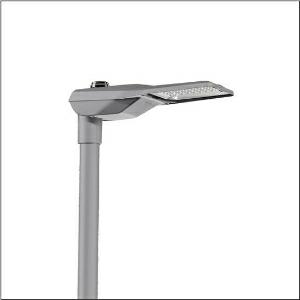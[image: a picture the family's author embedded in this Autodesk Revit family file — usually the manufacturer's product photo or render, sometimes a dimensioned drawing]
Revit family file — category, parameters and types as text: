
# Revit family: streetlight_sl_21_mini___stw1_0a_5xe6e37n08gb_9d35
name_source: partatom
category: Lighting Fixtures
units: mm (PartAtom-declared; Revit-internal decimal feet)

## family parameters
Cut with Voids When Loaded = No
Host = Face
Light Source = No
Part Type = Normal
Room Calculation Point = No
Round Connector Dimension = Use Diameter
Shared = No

## types (1)
- --- (1 x LED, 5940 lm, 40.4 W, 3000K)
    Apparent Load = 40 VA
    CIE Flux Codes = 38 75 98 100 100
    Color Rendering = 70
    Color Temperature = 3000K
    Default Elevation = 1800 mm
    Description = Streetlight SL 21 mini, mast luminaire, primary light control with lens, of PMMA, primary optical cover: cover, of toughened safety glass, transparent, light distribution: STW1.0a, light emission: direct distribution, primary light characteristic: asymmetric, installation type: side-entry, LED, 3G 1.5mm², High Power LED, rated luminous flux: 5.940lm, luminous efficacy: 147lm/W, light colour: 730, colour temperature: 3000K, control gear: NEMA (7pin), control: overheat protection, pre-setting: linear dimming characteristic, constant luminous flux control, time-dependent luminous flux control, flexible luminous flux parameterisation, mains connection: 230..240V, AC, 50/60Hz, connection cable pre-assembled, cable length: 8,5m, wiring characteristics: H07RN-F, start of lifetime: 40W, end of service life: 41W, reduction: 19W, luminaire housing, of diecast aluminium (EN AC-44300), powder-coated, SITECO metallic grey (DB 702S), corrosivity category C5 high according to DIN EN ISO 12944, multi-level sealing system, sealing non-destructively replaceable, inclination adjustable: 0°, 5°, 10°, 15°, length: 628mm, width: 235mm, height: 110mm, spigot size: 42mm (side-entry), mounting height: 4..8m, protection rating (complete): IP66, insulation class (complete): insulation class I (protective earthing), certification: CE, ENEC, ENEC+, VDE, impact resistance: IK10, permissible operating ambient temperature for outdoor applications: -40..+50°C, standard-compliant lighting for roads and squares, packaging unit: 1 piece

Light Distribution: STW1.0a
    Height = 110 mm
    Lamp = 1 x LED
    Lamp Light Flux = 5940 lm
    Lamp Power = 40.4 W
    Lamp count = 1
    Length = 625 mm
    Luminous efficacy = 147 lm/W
    Manufacturer = Siteco
    ModVariant = No
    Model = 5XE6E37N08GB
    Number of Poles = 1
    OnlyDefault = Yes
    Power Factor = 1
    Product Name = Streetlight SL 21 mini | STW1.0a
    Product group = mast luminaire | pylon top
    ProductGroupID = 6100
    Protection Class = Protection class I
    Protection Degree = IP 66
    RLX_Detail_Level = 1
    RLX_Emergency_Light_Flux = 0 lm
    RLX_Emergency_Type = 0
    RLX_Emergency_Type_DB = No
    RlxData = <blob elided: 25881 chars, md5=c4ef1062>
    Socket = socket
    Standby Power = 0 W
    System Light Flux = 5940 lm
    System Power = 40 W
    Type Comments = factory setting: luminous flux: 100 % | dim-lin: 254 | 812 mA
    Type Image = l_1294379.jpg
    URL = http://relux.com
    VarID = @adj_135211
    Voltage = 0 V
    Weight = 0.00 kg
    Width = 234 mm

## geometry (parser evidence)
native form markers: Blend x4, Sweep x12
no freeform markers — native parametric forms only
